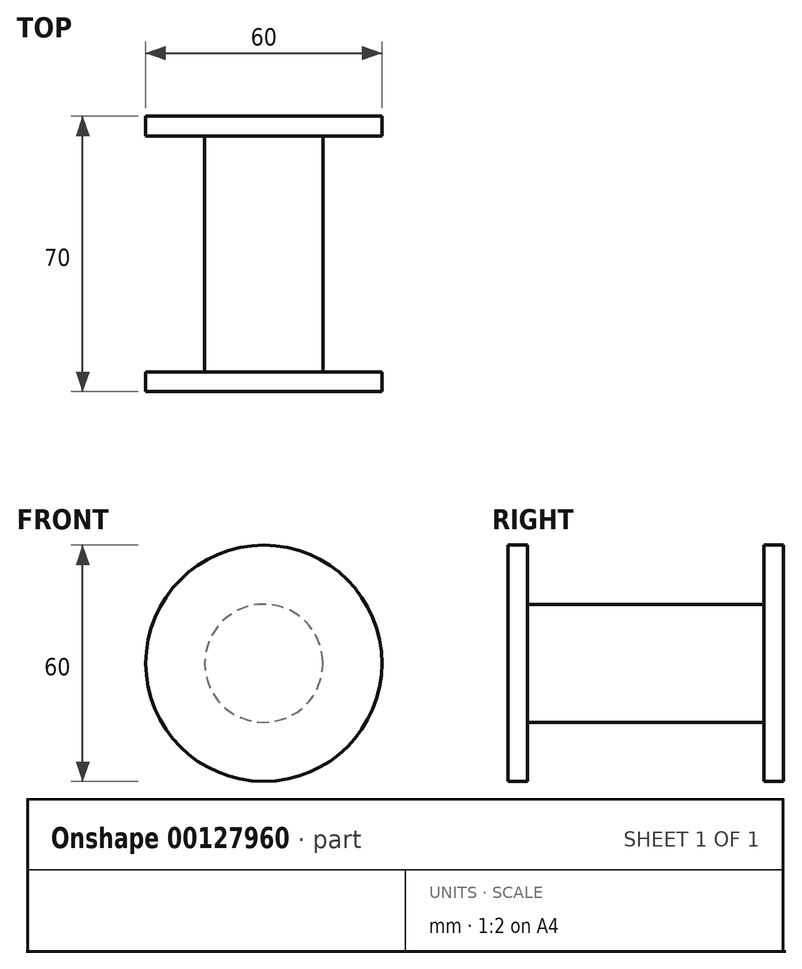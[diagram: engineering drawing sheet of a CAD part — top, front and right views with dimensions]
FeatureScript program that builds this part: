
annotation { "Feature Type Name" : "Feature", "Feature Type Description" : "" }
export const myFeature = defineFeature(function(context is Context, id is Id, definition is map)
    precondition{}
    {
        {
            var Q0;
            Q0=qCreatedBy(makeId("Top.planeOp"),FACE);
            var sketch = newSketch(context, id + "F0", { "sketchPlane" : qUnion([Q0])});
            skLineSegment(sketch, "E0", {"start": v(0, 0) * mm, "end": v(0, 70) * mm});
            skLineSegment(sketch, "E1", {"start": v(0, 70) * mm, "end": v(30, 70) * mm});
            skLineSegment(sketch, "E2", {"start": v(30, 70) * mm, "end": v(30, 65) * mm});
            skLineSegment(sketch, "E3", {"start": v(30, 65) * mm, "end": v(15, 65) * mm});
            skLineSegment(sketch, "E4", {"start": v(15, 65) * mm, "end": v(15, 5) * mm});
            skLineSegment(sketch, "E5", {"start": v(15, 5) * mm, "end": v(30, 5) * mm});
            skLineSegment(sketch, "E6", {"start": v(30, 5) * mm, "end": v(30, 0) * mm});
            skLineSegment(sketch, "E7", {"start": v(30, 0) * mm, "end": v(0, 0) * mm});
            skLineSegment(sketch, "E8", {"start": v(0, 70) * mm, "end": v(0, 86.83) * mm});
            skSolve(sketch);
        }
        {
            var Q0;
            Q0=makeQuery(id+"F0.imprint","IMPRINT",FACE,{"disambiguationData":[TD([[makeQuery(id+"F0.imprint","IMPRINT",EDGE,{"derivedFrom":sQuery(id+"F0.wireOp",EDGE,"E0")}),-1.0]])]});
            var Q1;
            Q1=sQuery(id+"F0.wireOp",EDGE,"E8");
            revolve(context, id + "F1", {"entities" : qUnion([Q0]), "axis" : qUnion([Q1]), "revolveType" : RevolveType.FULL});
        }
    });
